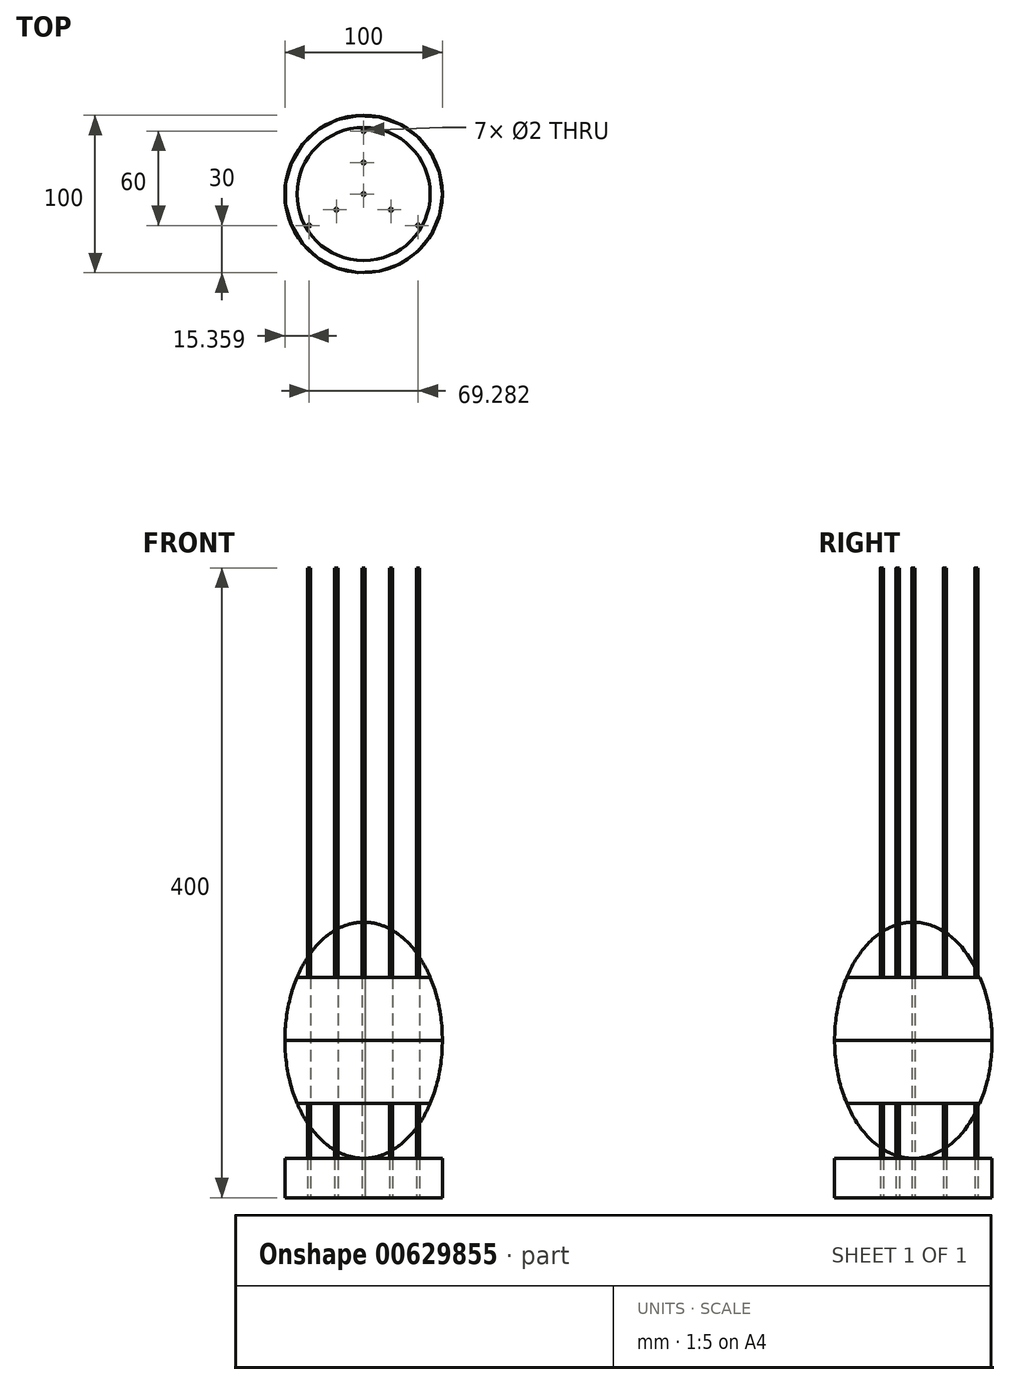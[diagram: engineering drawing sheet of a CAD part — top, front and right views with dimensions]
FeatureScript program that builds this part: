
annotation { "Feature Type Name" : "Feature", "Feature Type Description" : "" }
export const myFeature = defineFeature(function(context is Context, id is Id, definition is map)
    precondition{}
    {
        {
            var Q0;
            Q0=qCreatedBy(makeId("Top.planeOp"),FACE);
            var sketch = newSketch(context, id + "F0", { "sketchPlane" : qUnion([Q0])});
            skCircle(sketch, "E0", {"center": v(0, 0) * mm, "radius": 50 * mm, "construction": true});
            skCircle(sketch, "E1", {"center": v(0, 40) * mm, "radius": 1 * mm});
            skCircle(sketch, "E2.1.0.0", {"center": v(0, 20) * mm, "radius": 1 * mm});
            skLineSegment(sketch, "E2.direction1", {"start": v(0, 40) * mm, "end": v(0, 20) * mm, "construction": true});
            skCircle(sketch, "E3.1.0", {"center": v(-17.32, -10) * mm, "radius": 1 * mm});
            skCircle(sketch, "E3.1.1", {"center": v(-34.64, -20) * mm, "radius": 1 * mm});
            skCircle(sketch, "E3.2.0", {"center": v(17.32, -10) * mm, "radius": 1 * mm});
            skCircle(sketch, "E3.2.1", {"center": v(34.64, -20) * mm, "radius": 1 * mm});
            skCircle(sketch, "E4", {"center": v(0, 0) * mm, "radius": 1 * mm});
            skSolve(sketch);
        }
        {
            var Q0;
            Q0=qCreatedBy(makeId("Top.planeOp"),FACE);
            var sketch = newSketch(context, id + "F1", { "sketchPlane" : qUnion([Q0])});
            skCircle(sketch, "E5", {"center": v(0, 0) * mm, "radius": 50 * mm});
            skSolve(sketch);
        }
        {
            var Q0;
            Q0 = qSketchRegion(id + "F1", true);
            extrude(context, id + "F2", {"entities" : qUnion([Q0]), "depth" : 25 * mm, "offsetDistance" : 25 * mm});
        }
        {
            var Q0;
            Q0 = qSketchRegion(id + "F0", true);
            extrude(context, id + "F3", {"entities" : qUnion([Q0]), "operationType" : NewBodyOperationType.REMOVE, "depth" : 200 * mm, "offsetDistance" : 25 * mm});
        }
        {
            var Q0;
            Q0 = qSketchRegion(id + "F0", true);
            extrude(context, id + "F4", {"entities" : qUnion([Q0]), "depth" : 400 * mm, "offsetDistance" : 25 * mm});
        }
        {
            var Q0;
            Q0=qCreatedBy(makeId("Front.planeOp"),FACE);
            var sketch = newSketch(context, id + "F5", { "sketchPlane" : qUnion([Q0])});
            skEllipse(sketch, "E6", {"center": v(0, 100) * mm, "majorRadius": 75 * mm, "minorRadius": 50 * mm, "majorAxis": v(0, -1)});
            skLineSegment(sketch, "E7", {"start": v(-42.3, 60) * mm, "end": v(42.3, 60) * mm});
            skLineSegment(sketch, "E8", {"start": v(-50, 100) * mm, "end": v(50, 100) * mm});
            skLineSegment(sketch, "E9.MirrorCS", {"start": v(-42.3, 140) * mm, "end": v(42.3, 140) * mm});
            skLineSegment(sketch, "E10", {"start": v(0, 25) * mm, "end": v(0, 237.57) * mm, "construction": true});
            skPoint(sketch, "E10.endSnap0", {"position": v(0, 175) * mm});
            skLineSegment(sketch, "E11", {"start": v(0, 175) * mm, "end": v(0, 25) * mm});
            skSolve(sketch);
        }
        {
            var Q0;
            {var subQ0=sQuery(id+"F5.wireOp",EDGE,"E9.MirrorCS");var subQ1=sQuery(id+"F5.wireOp",EDGE,"E6");var subQ2=makeQuery(id+"F5.imprint","INTERSECT",VERTEX,{"disambiguationData":[OD(1.0)],"derivedFrom":[subQ1,subQ0]});Q0=makeQuery(id+"F5.imprint","IMPRINT",FACE,{"disambiguationData":[TD([[makeQuery(id+"F5.imprint","IMPRINT",EDGE,{"disambiguationData":[TD([[subQ2,-1.0]])],"derivedFrom":subQ1}),1.0]])]});}
            var Q1;
            Q1=sQuery(id+"F5.wireOp",EDGE,"E10");
            revolve(context, id + "F6", {"entities" : qUnion([Q0]), "axis" : qUnion([Q1]), "revolveType" : RevolveType.FULL});
        }
        {
            var Q0;
            {var subQ0=sQuery(id+"F5.wireOp",EDGE,"E8");var subQ1=sQuery(id+"F5.wireOp",EDGE,"E6");var subQ2=makeQuery(id+"F5.imprint","INTERSECT",VERTEX,{"disambiguationData":[OD(1.0)],"derivedFrom":[subQ1,subQ0]});Q0=makeQuery(id+"F5.imprint","IMPRINT",FACE,{"disambiguationData":[TD([[makeQuery(id+"F5.imprint","IMPRINT",EDGE,{"disambiguationData":[TD([[subQ2,-1.0]])],"derivedFrom":subQ1}),1.0]])]});}
            var Q1;
            Q1=sQuery(id+"F5.wireOp",EDGE,"E11");
            revolve(context, id + "F7", {"entities" : qUnion([Q0]), "axis" : qUnion([Q1]), "revolveType" : RevolveType.FULL});
        }
        {
            var Q0;
            {var subQ0=sQuery(id+"F5.wireOp",EDGE,"E7");var subQ1=sQuery(id+"F5.wireOp",EDGE,"E6");var subQ2=makeQuery(id+"F5.imprint","INTERSECT",VERTEX,{"disambiguationData":[OD(1.0)],"derivedFrom":[subQ1,subQ0]});Q0=makeQuery(id+"F5.imprint","IMPRINT",FACE,{"disambiguationData":[TD([[makeQuery(id+"F5.imprint","IMPRINT",EDGE,{"disambiguationData":[TD([[subQ2,-1.0]])],"derivedFrom":subQ1}),1.0]])]});}
            var Q1;
            Q1=sQuery(id+"F5.wireOp",EDGE,"E11");
            revolve(context, id + "F8", {"entities" : qUnion([Q0]), "axis" : qUnion([Q1]), "revolveType" : RevolveType.FULL});
        }
        {
            var Q0;
            {var subQ0=sQuery(id+"F5.wireOp",EDGE,"E7");var subQ1=sQuery(id+"F5.wireOp",EDGE,"E6");var subQ2=makeQuery(id+"F5.imprint","INTERSECT",VERTEX,{"disambiguationData":[OD(1.0)],"derivedFrom":[subQ1,subQ0]});Q0=makeQuery(id+"F5.imprint","IMPRINT",FACE,{"disambiguationData":[TD([[makeQuery(id+"F5.imprint","IMPRINT",EDGE,{"disambiguationData":[TD([[subQ2,1.0]])],"derivedFrom":subQ1}),1.0]])]});}
            var Q1;
            Q1=sQuery(id+"F5.wireOp",EDGE,"E11");
            revolve(context, id + "F9", {"entities" : qUnion([Q0]), "axis" : qUnion([Q1]), "revolveType" : RevolveType.FULL});
        }
    });
